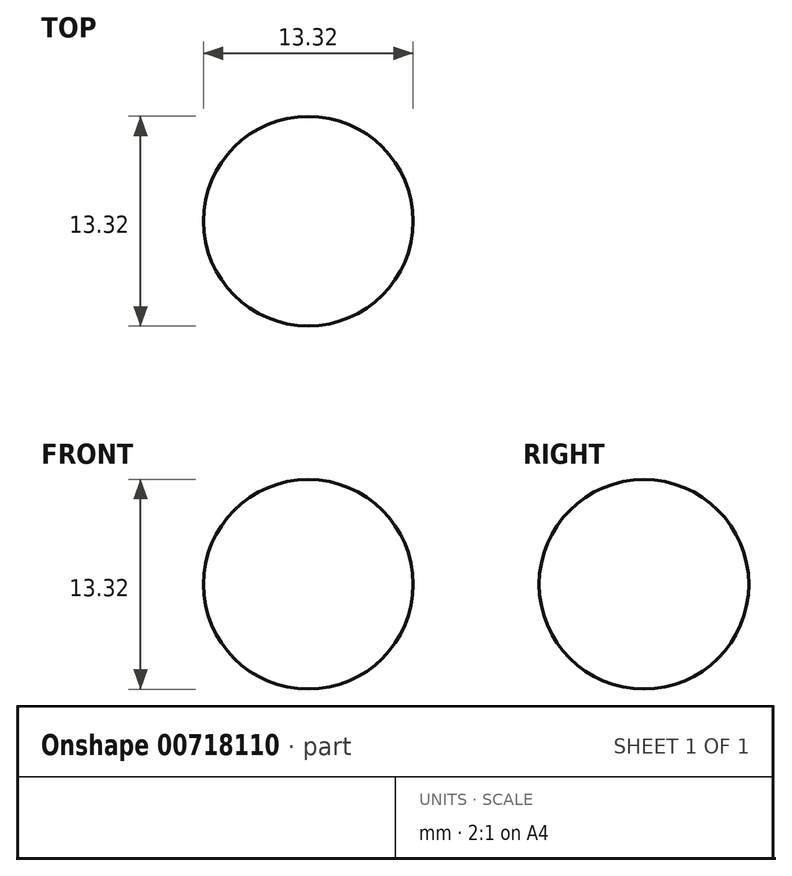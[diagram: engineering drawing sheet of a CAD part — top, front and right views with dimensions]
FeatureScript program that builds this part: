
annotation { "Feature Type Name" : "Feature", "Feature Type Description" : "" }
export const myFeature = defineFeature(function(context is Context, id is Id, definition is map)
    precondition{}
    {
        {
            var Q0;
            Q0=qCreatedBy(makeId("Top.planeOp"),FACE);
            var sketch = newSketch(context, id + "F0", { "sketchPlane" : qUnion([Q0])});
            skCircle(sketch, "E0", {"center": v(0, 0) * mm, "radius": 6.66 * mm});
            skLineSegment(sketch, "E1", {"start": v(0, 6.66) * mm, "end": v(0, -6.66) * mm});
            skSolve(sketch);
        }
        {
            var Q0;
            {var subQ0=sQuery(id+"F0.wireOp",EDGE,"E1");Q0=makeQuery(id+"F0.imprint","IMPRINT",FACE,{"disambiguationData":[TD([[makeQuery(id+"F0.imprint","IMPRINT",EDGE,{"derivedFrom":subQ0}),1.0]])]});}
            var Q1;
            Q1=sQuery(id+"F0.wireOp",EDGE,"E1");
            revolve(context, id + "F1", {"surfaceOperationType" : NewSurfaceOperationType.NEW, "entities" : qUnion([Q0]), "axis" : qUnion([Q1]), "revolveType" : RevolveType.FULL});
        }
    });
